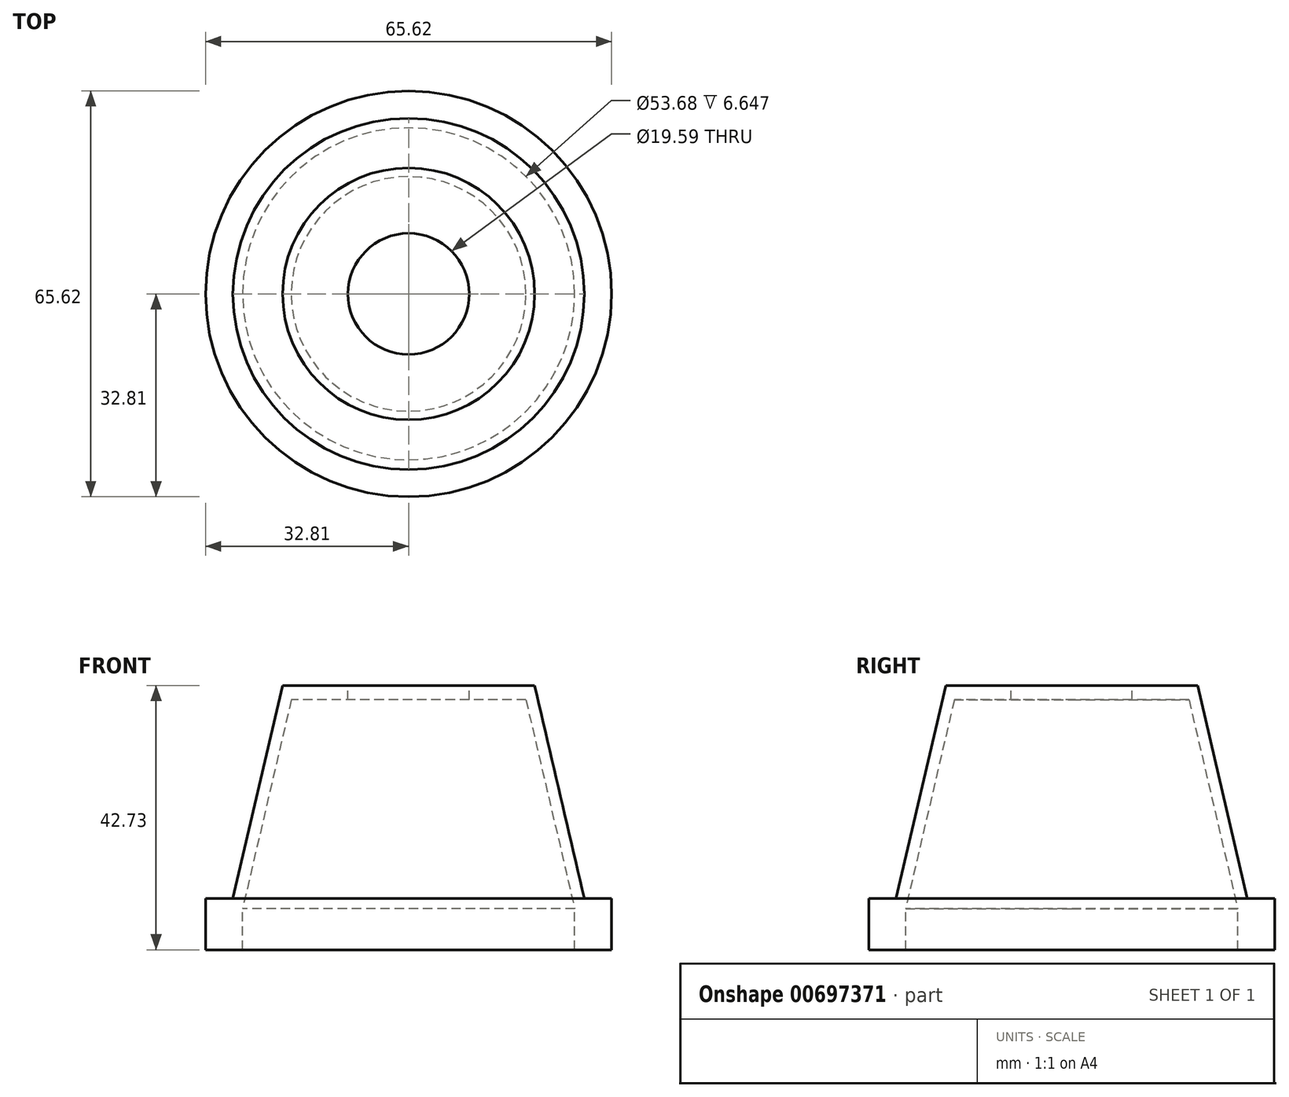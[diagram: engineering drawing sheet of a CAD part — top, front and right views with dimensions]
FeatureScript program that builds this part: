
annotation { "Feature Type Name" : "Feature", "Feature Type Description" : "" }
export const myFeature = defineFeature(function(context is Context, id is Id, definition is map)
    precondition{}
    {
        {
            var Q0;
            Q0=qCreatedBy(makeId("Front.planeOp"),FACE);
            var sketch = newSketch(context, id + "F0", { "sketchPlane" : qUnion([Q0])});
            skLineSegment(sketch, "E0", {"start": v(-32.8, 0) * mm, "end": v(-32.8, 8.32) * mm});
            skLineSegment(sketch, "E1", {"start": v(-32.8, 8.32) * mm, "end": v(-28.4, 8.32) * mm});
            skLineSegment(sketch, "E2", {"start": v(-28.4, 8.32) * mm, "end": v(-20.36, 42.73) * mm});
            skLineSegment(sketch, "E3", {"start": v(-20.36, 42.73) * mm, "end": v(-9.8, 42.73) * mm});
            skLineSegment(sketch, "E4", {"start": v(-9.8, 42.73) * mm, "end": v(-9.8, 40.4) * mm});
            skLineSegment(sketch, "E5", {"start": v(-9.8, 40.4) * mm, "end": v(-18.96, 40.4) * mm});
            skLineSegment(sketch, "E6", {"start": v(-32.8, 0) * mm, "end": v(-26.84, 0) * mm});
            skLineSegment(sketch, "E7", {"start": v(-26.84, 0) * mm, "end": v(-26.84, 6.65) * mm});
            skLineSegment(sketch, "E8", {"start": v(-26.84, 6.65) * mm, "end": v(-18.96, 40.4) * mm});
            skLineSegment(sketch, "E9", {"start": v(0, 53.61) * mm, "end": v(0, 0) * mm});
            skSolve(sketch);
        }
        {
            var Q0;
            Q0=makeQuery(id+"F0.imprint","IMPRINT",FACE,{"disambiguationData":[TD([[makeQuery(id+"F0.imprint","IMPRINT",EDGE,{"derivedFrom":sQuery(id+"F0.wireOp",EDGE,"E0")}),-1.0]])]});
            var Q1;
            Q1=sQuery(id+"F0.wireOp",EDGE,"E9");
            revolve(context, id + "F1", {"entities" : qUnion([Q0]), "axis" : qUnion([Q1]), "revolveType" : RevolveType.FULL});
        }
    });
